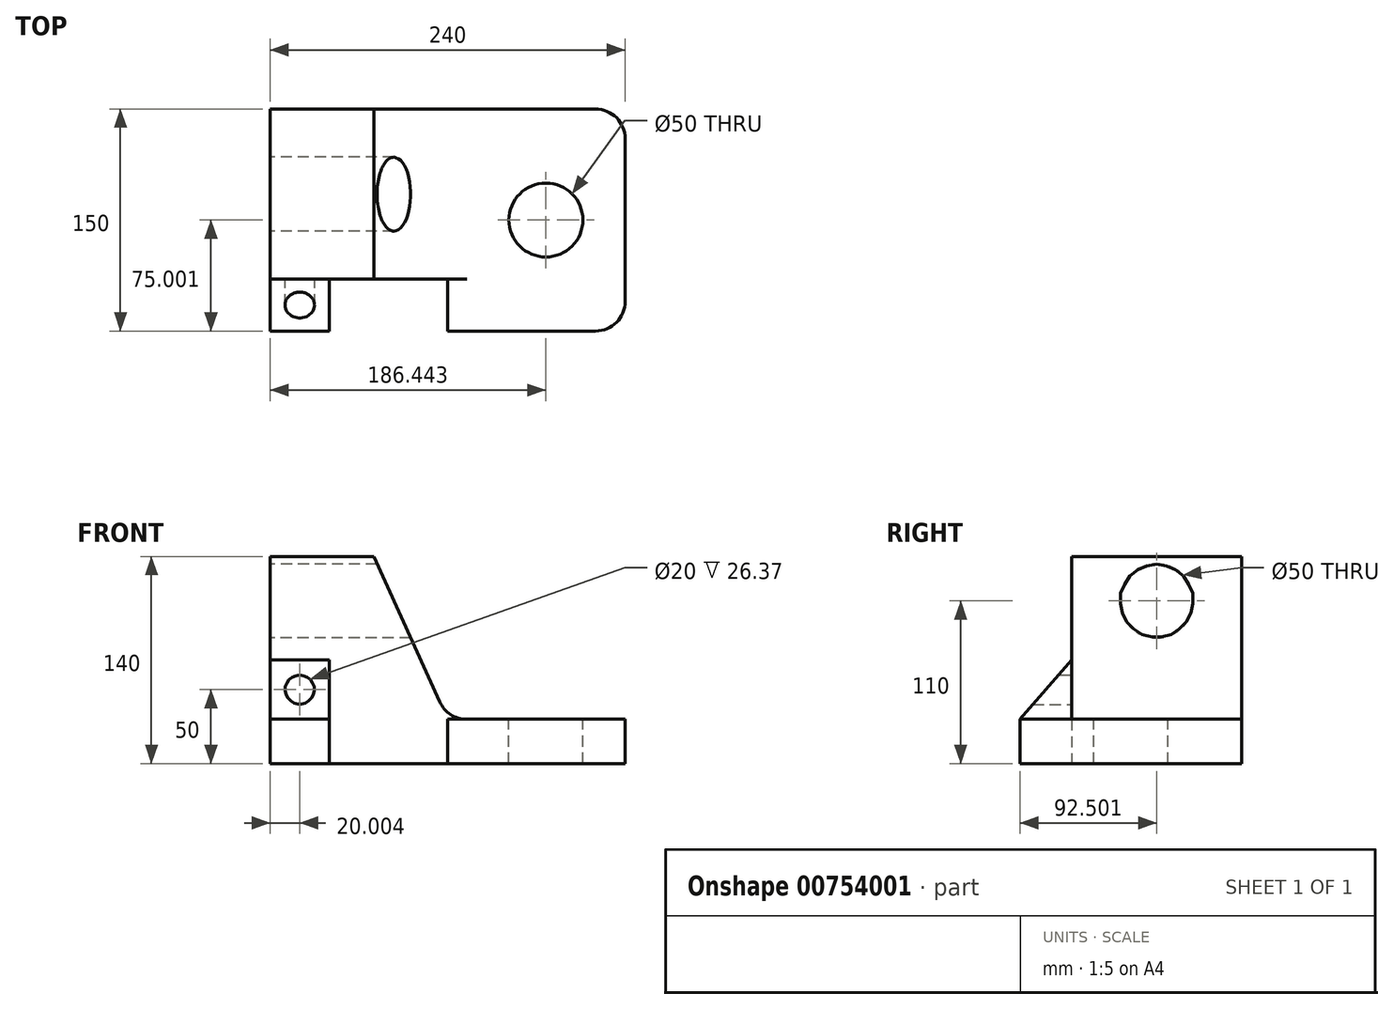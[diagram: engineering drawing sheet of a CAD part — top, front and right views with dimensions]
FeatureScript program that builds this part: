
annotation { "Feature Type Name" : "Feature", "Feature Type Description" : "" }
export const myFeature = defineFeature(function(context is Context, id is Id, definition is map)
    precondition{}
    {
        {
            var Q0;
            Q0=qCreatedBy(makeId("Top.planeOp"),FACE);
            var sketch = newSketch(context, id + "F0", { "sketchPlane" : qUnion([Q0])});
            skLineSegment(sketch, "E0", {"start": v(-67.25, 134.32) * mm, "end": v(-67.25, -15.68) * mm});
            skLineSegment(sketch, "E1", {"start": v(-67.25, 134.32) * mm, "end": v(172.75, 134.32) * mm});
            skLineSegment(sketch, "E2", {"start": v(172.75, 134.32) * mm, "end": v(172.75, -15.68) * mm});
            skLineSegment(sketch, "E3", {"start": v(172.75, -15.68) * mm, "end": v(52.75, -15.68) * mm});
            skLineSegment(sketch, "E4", {"start": v(52.75, -15.68) * mm, "end": v(52.75, 19.32) * mm});
            skLineSegment(sketch, "E5", {"start": v(-67.25, -15.68) * mm, "end": v(-27.25, -15.68) * mm});
            skLineSegment(sketch, "E6", {"start": v(-27.25, -15.68) * mm, "end": v(-27.25, 19.32) * mm});
            skLineSegment(sketch, "E7", {"start": v(-27.25, 19.32) * mm, "end": v(52.75, 19.32) * mm});
            skSolve(sketch);
        }
        {
            var Q0;
            Q0=makeQuery(id+"F0.imprint","IMPRINT",FACE,{"disambiguationData":[TD([[makeQuery(id+"F0.imprint","IMPRINT",EDGE,{"derivedFrom":sQuery(id+"F0.wireOp",EDGE,"E0")}),1.0]])]});
            var sketch = newSketch(context, id + "F1", { "sketchPlane" : qUnion([Q0])});
            skLineSegment(sketch, "E8.0.0", {"start": v(-27.25, -15.68) * mm, "end": v(-27.25, 19.32) * mm});
            skLineSegment(sketch, "E8.0.1", {"start": v(-27.25, 19.32) * mm, "end": v(52.75, 19.32) * mm});
            skLineSegment(sketch, "E8.0.2", {"start": v(52.75, 19.32) * mm, "end": v(52.75, -15.68) * mm});
            skLineSegment(sketch, "E8.0.3", {"start": v(52.75, -15.68) * mm, "end": v(172.75, -15.68) * mm});
            skLineSegment(sketch, "E8.0.4", {"start": v(172.75, -15.68) * mm, "end": v(172.75, 134.32) * mm});
            skLineSegment(sketch, "E8.0.5", {"start": v(172.75, 134.32) * mm, "end": v(-67.25, 134.32) * mm});
            skLineSegment(sketch, "E8.0.6", {"start": v(-67.25, 134.32) * mm, "end": v(-67.25, -15.68) * mm});
            skLineSegment(sketch, "E8.0.7", {"start": v(-67.25, -15.68) * mm, "end": v(-27.25, -15.68) * mm});
            skLineSegment(sketch, "E9", {"start": v(-67.25, 19.32) * mm, "end": v(172.75, 19.32) * mm});
            skSolve(sketch);
        }
        {
            var Q0;
            {var subQ0=sQuery(id+"F1.wireOp",EDGE,"E8.0.0");Q0=makeQuery(id+"F1.imprint","IMPRINT",FACE,{"disambiguationData":[TD([[makeQuery(id+"F1.imprint","IMPRINT",EDGE,{"derivedFrom":subQ0}),1.0]])]});}
            extrude(context, id + "F2", {"entities" : qUnion([Q0]), "depth" : 70 * mm, "offsetDistance" : 25 * mm});
        }
        {
            var Q0;
            Q0=makeQuery(id+"F0.imprint","IMPRINT",FACE,{"disambiguationData":[TD([[makeQuery(id+"F0.imprint","IMPRINT",EDGE,{"derivedFrom":sQuery(id+"F0.wireOp",EDGE,"E0")}),1.0]])]});
            extrude(context, id + "F3", {"entities" : qUnion([Q0]), "operationType" : NewBodyOperationType.ADD, "depth" : 30 * mm, "offsetDistance" : 25 * mm});
        }
        {
            var Q0;
            Q0=makeQuery(id+"F2.opExtrude","SWEPT_FACE",FACE,{"disambiguationData":[OSD([sQuery(id+"F1.wireOp",EDGE,"E8.0.0")])]});
            var sketch = newSketch(context, id + "F4", { "sketchPlane" : qUnion([Q0])});
            skLineSegment(sketch, "E10", {"start": v(-15.68, 0) * mm, "end": v(-15.68, 30) * mm});
            skLineSegment(sketch, "E11", {"start": v(-15.68, 30) * mm, "end": v(19.32, 70) * mm});
            skSolve(sketch);
        }
        {
            var Q0;
            Q0 = qSketchRegion(id + "F4", true);
            var Q1;
            {var subQ0=sQuery(id+"F4.wireOp",EDGE,"E11");Q1=makeQuery(id+"F4.imprint","IMPRINT",FACE,{"disambiguationData":[TD([[makeQuery(id+"F4.imprint","IMPRINT",EDGE,{"derivedFrom":subQ0}),1.0]])]});}
            extrude(context, id + "F5", {"entities" : qUnion([Q0, Q1]), "operationType" : NewBodyOperationType.REMOVE, "oppositeDirection" : true, "depth" : 103 * mm, "offsetDistance" : 25 * mm});
        }
        {
            var Q0;
            Q0=makeQuery(id+"F3.opExtrude","SWEPT_EDGE",EDGE,{"disambiguationData":[OSD([sQuery(id+"F0.wireOp",EDGE,"E2"),sQuery(id+"F0.wireOp",EDGE,"E3")])]});
            var Q1;
            Q1=makeQuery(id+"F3.opExtrude","SWEPT_EDGE",EDGE,{"disambiguationData":[OSD([sQuery(id+"F0.wireOp",EDGE,"E1"),sQuery(id+"F0.wireOp",EDGE,"E2")])]});
            fillet(context, id + "F6", {"entities" : qUnion([Q0, Q1]), "radius" : 20 * mm, "tangentPropagation" : true, "allowEdgeOverflow" : false});
        }
        {
            var Q0;
            Q0=makeQuery(id+"F2.opExtrude","SWEPT_FACE",FACE,{"disambiguationData":[OSD([sQuery(id+"F1.wireOp",EDGE,"E9")])]});
            var sketch = newSketch(context, id + "F7", { "sketchPlane" : qUnion([Q0])});
            skLineSegment(sketch, "E12", {"start": v(47.25, 70) * mm, "end": v(47.25, 30) * mm});
            skCircle(sketch, "E13", {"center": v(47.25, 50) * mm, "radius": 10 * mm});
            skSolve(sketch);
        }
        {
            var Q0;
            Q0 = qSketchRegion(id + "F7", true);
            extrude(context, id + "F8", {"entities" : qUnion([Q0]), "operationType" : NewBodyOperationType.REMOVE, "oppositeDirection" : true, "depth" : 28 * mm, "offsetDistance" : 25 * mm});
        }
        {
            var Q0;
            Q0=makeQuery(id+"F3.boolean.opBoolean","MERGE",FACE,{"derivedFrom":[makeQuery(id+"F2.opExtrude","CAP_FACE",FACE,{"disambiguationData":[OSD([sQuery(id+"F1.wireOp",EDGE,"E8.0.0"),sQuery(id+"F1.wireOp",EDGE,"E8.0.6"),sQuery(id+"F1.wireOp",EDGE,"E8.0.7"),sQuery(id+"F1.wireOp",EDGE,"E9")])],"isStart":true}),makeQuery(id+"F3.opExtrude","CAP_FACE",FACE,{"disambiguationData":[OSD([sQuery(id+"F0.wireOp",EDGE,"E0"),sQuery(id+"F0.wireOp",EDGE,"E1"),sQuery(id+"F0.wireOp",EDGE,"E2"),sQuery(id+"F0.wireOp",EDGE,"E3"),sQuery(id+"F0.wireOp",EDGE,"E4"),sQuery(id+"F0.wireOp",EDGE,"E5"),sQuery(id+"F0.wireOp",EDGE,"E6"),sQuery(id+"F0.wireOp",EDGE,"E7")])],"isStart":true})]});
            var sketch = newSketch(context, id + "F9", { "sketchPlane" : qUnion([Q0])});
            skLineSegment(sketch, "E14", {"start": v(52.75, -19.32) * mm, "end": v(52.75, -134.32) * mm});
            skLineSegment(sketch, "E15", {"start": v(-27.25, -19.32) * mm, "end": v(-67.25, -19.32) * mm});
            skSolve(sketch);
        }
        {
            var Q0;
            {var subQ4=sQuery(id+"F9.wireOp",EDGE,"E14");Q0=makeQuery(id+"F9.imprint","IMPRINT",FACE,{"disambiguationData":[TD([[makeQuery(id+"F9.imprint","IMPRINT",EDGE,{"derivedFrom":subQ4}),-1.0]])]});}
            extrude(context, id + "F10", {"entities" : qUnion([Q0]), "operationType" : NewBodyOperationType.ADD, "oppositeDirection" : true, "depth" : 140 * mm, "offsetDistance" : 25 * mm});
        }
        {
            var Q0;
            {var subQ0=sQuery(id+"F0.wireOp",EDGE,"E7");Q0=makeQuery(id+"F10.boolean.opBoolean","MERGE",FACE,{"derivedFrom":[makeQuery(id+"F3.opExtrude","SWEPT_FACE",FACE,{"disambiguationData":[OSD([subQ0])]}),makeQuery(id+"F10.opExtrude","SWEPT_FACE",FACE,{"disambiguationData":[OSD([subQ0,sQuery(id+"F9.wireOp",EDGE,"E15")])]})]});}
            var sketch = newSketch(context, id + "F11", { "sketchPlane" : qUnion([Q0])});
            skLineSegment(sketch, "E16", {"start": v(-67.25, 140) * mm, "end": v(2.75, 140) * mm});
            skLineSegment(sketch, "E17", {"start": v(2.75, 140) * mm, "end": v(52.75, 30) * mm});
            skSolve(sketch);
        }
        {
            var Q0;
            {var subQ0=sQuery(id+"F11.wireOp",EDGE,"E17");Q0=makeQuery(id+"F11.imprint","IMPRINT",FACE,{"disambiguationData":[TD([[makeQuery(id+"F11.imprint","IMPRINT",EDGE,{"derivedFrom":subQ0}),1.0]])]});}
            extrude(context, id + "F12", {"entities" : qUnion([Q0]), "operationType" : NewBodyOperationType.REMOVE, "oppositeDirection" : true, "depth" : 1016 * mm, "offsetDistance" : 25 * mm});
        }
        {
            var Q0;
            {var subQ0=sQuery(id+"F9.wireOp",EDGE,"E14");var subQ1=sQuery(id+"F0.wireOp",EDGE,"E7");var subQ2=sQuery(id+"F0.wireOp",EDGE,"E4");Q0=makeQuery(id+"F12.boolean.opBoolean","MERGE",EDGE,{"derivedFrom":[makeQuery(id+"F10.boolean.opBoolean","INTERSECT",EDGE,{"derivedFrom":[makeQuery(id+"F3.opExtrude","CAP_FACE",FACE,{"disambiguationData":[OSD([sQuery(id+"F0.wireOp",EDGE,"E0"),sQuery(id+"F0.wireOp",EDGE,"E1"),sQuery(id+"F0.wireOp",EDGE,"E2"),sQuery(id+"F0.wireOp",EDGE,"E3"),subQ2,sQuery(id+"F0.wireOp",EDGE,"E5"),sQuery(id+"F0.wireOp",EDGE,"E6"),subQ1])],"isStart":false}),makeQuery(id+"F10.opExtrude","SWEPT_FACE",FACE,{"disambiguationData":[OSD([subQ0])]})]}),makeQuery(id+"F12.opExtrude","SWEPT_EDGE",EDGE,{"disambiguationData":[OSD([subQ2,subQ1,subQ0,sQuery(id+"F11.wireOp",EDGE,"E17")])]})]});}
            fillet(context, id + "F13", {"entities" : qUnion([Q0]), "radius" : 20 * mm, "tangentPropagation" : true, "allowEdgeOverflow" : false});
        }
        {
            var Q0;
            Q0=makeQuery(id+"F3.opExtrude","CAP_FACE",FACE,{"disambiguationData":[OSD([sQuery(id+"F0.wireOp",EDGE,"E0"),sQuery(id+"F0.wireOp",EDGE,"E1"),sQuery(id+"F0.wireOp",EDGE,"E2"),sQuery(id+"F0.wireOp",EDGE,"E3"),sQuery(id+"F0.wireOp",EDGE,"E4"),sQuery(id+"F0.wireOp",EDGE,"E5"),sQuery(id+"F0.wireOp",EDGE,"E6"),sQuery(id+"F0.wireOp",EDGE,"E7")])],"isStart":false});
            var sketch = newSketch(context, id + "F14", { "sketchPlane" : qUnion([Q0])});
            skLineSegment(sketch, "E18", {"start": v(172.75, 59.32) * mm, "end": v(65.63, 59.32) * mm});
            skCircle(sketch, "E19", {"center": v(119.2, 59.32) * mm, "radius": 25 * mm});
            skSolve(sketch);
        }
        {
            var Q0;
            Q0 = qSketchRegion(id + "F14", true);
            extrude(context, id + "F15", {"entities" : qUnion([Q0]), "operationType" : NewBodyOperationType.REMOVE, "oppositeDirection" : true, "depth" : 80 * mm, "offsetDistance" : 25 * mm});
        }
        {
            var Q0;
            {var subQ0=sQuery(id+"F1.wireOp",EDGE,"E8.0.6");var subQ1=sQuery(id+"F0.wireOp",EDGE,"E0");Q0=makeQuery(id+"F10.boolean.opBoolean","MERGE",FACE,{"derivedFrom":[makeQuery(id+"F3.boolean.opBoolean","MERGE",FACE,{"derivedFrom":[makeQuery(id+"F2.opExtrude","SWEPT_FACE",FACE,{"disambiguationData":[OSD([subQ0])]}),makeQuery(id+"F3.opExtrude","SWEPT_FACE",FACE,{"disambiguationData":[OSD([subQ1])]})]}),makeQuery(id+"F10.opExtrude","SWEPT_FACE",FACE,{"disambiguationData":[OSD([subQ1,subQ0])]})]});}
            var sketch = newSketch(context, id + "F16", { "sketchPlane" : qUnion([Q0])});
            skLineSegment(sketch, "E20", {"start": v(-76.82, 140) * mm, "end": v(-76.82, 110) * mm});
            skCircle(sketch, "E21", {"center": v(-76.82, 110) * mm, "radius": 25 * mm});
            skSolve(sketch);
        }
        {
            var Q0;
            Q0 = qSketchRegion(id + "F16", true);
            extrude(context, id + "F17", {"entities" : qUnion([Q0]), "operationType" : NewBodyOperationType.REMOVE, "oppositeDirection" : true, "depth" : 396 * mm, "offsetDistance" : 25 * mm});
        }
    });
